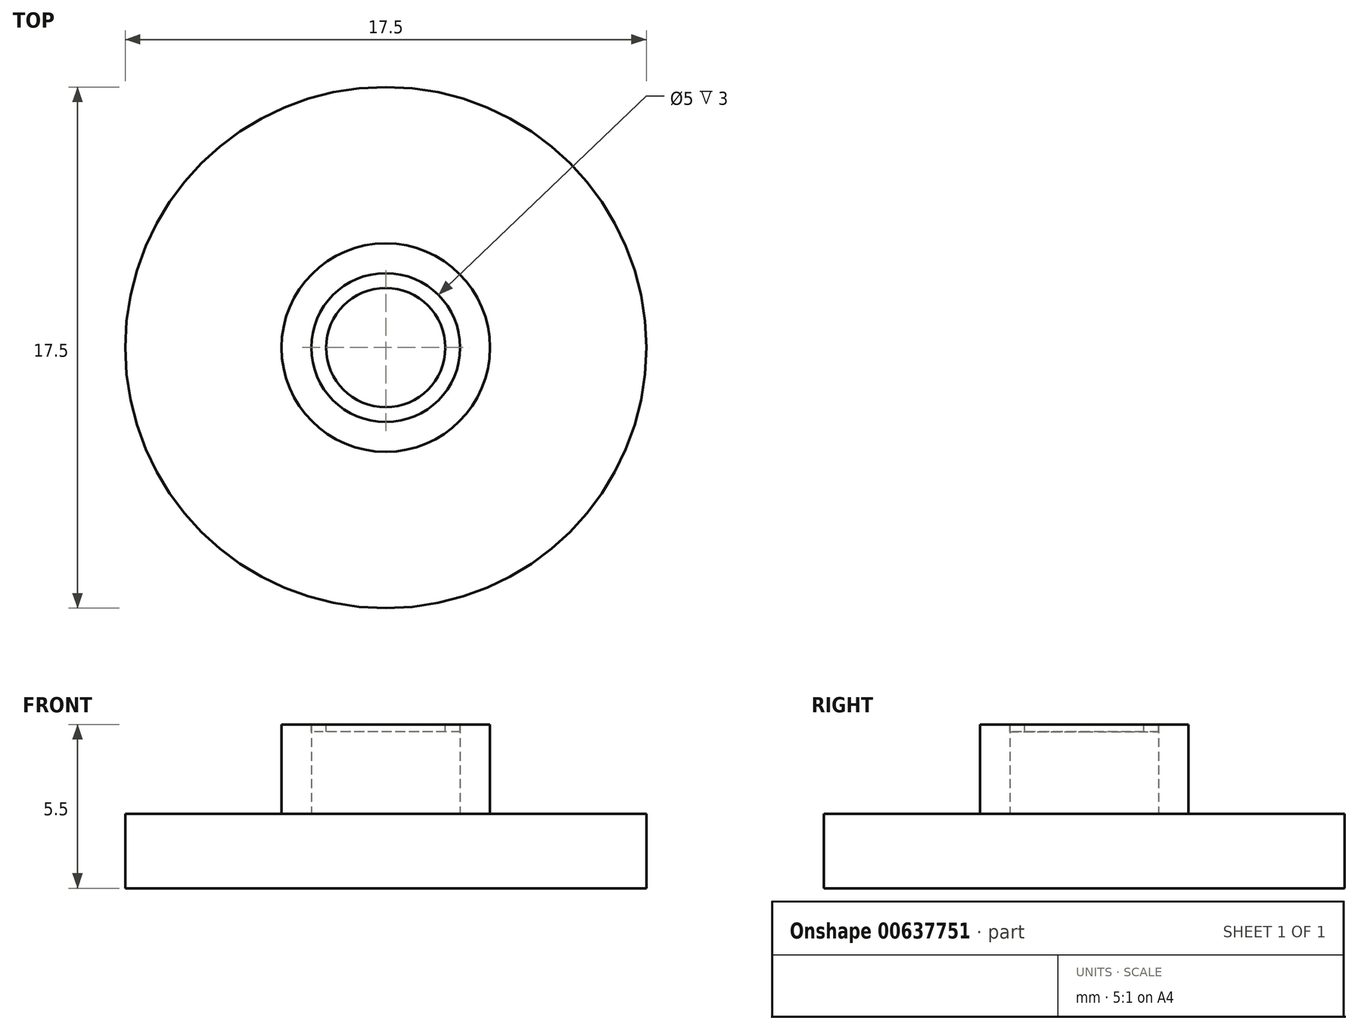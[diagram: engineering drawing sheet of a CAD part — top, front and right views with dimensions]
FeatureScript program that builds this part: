
annotation { "Feature Type Name" : "Feature", "Feature Type Description" : "" }
export const myFeature = defineFeature(function(context is Context, id is Id, definition is map)
    precondition{}
    {
        {
            var Q0;
            Q0=qCreatedBy(makeId("Top.planeOp"),FACE);
            var sketch = newSketch(context, id + "F0", { "sketchPlane" : qUnion([Q0])});
            skCircle(sketch, "E0", {"center": v(0, 0) * mm, "radius": 8.75 * mm});
            skSolve(sketch);
        }
        {
            var Q0;
            Q0=makeQuery(id+"F0.imprint","IMPRINT",FACE,{"disambiguationData":[TD([[makeQuery(id+"F0.imprint","IMPRINT",EDGE,{"derivedFrom":sQuery(id+"F0.wireOp",EDGE,"E0")}),1.0]])]});
            extrude(context, id + "F1", {"entities" : qUnion([Q0]), "depth" : 2.5 * mm, "offsetDistance" : 25.4 * mm});
        }
        {
            var Q0;
            Q0=makeQuery(id+"F1.opExtrude","CAP_FACE",FACE,{"disambiguationData":[OSD([sQuery(id+"F0.wireOp",EDGE,"E0")])],"isStart":false});
            var sketch = newSketch(context, id + "F2", { "sketchPlane" : qUnion([Q0])});
            skCircle(sketch, "E1", {"center": v(0, 0) * mm, "radius": 3.5 * mm});
            skCircle(sketch, "E2", {"center": v(0, 0) * mm, "radius": 2.5 * mm});
            skSolve(sketch);
        }
        {
            var Q0;
            Q0=makeQuery(id+"F2.imprint","IMPRINT",FACE,{"disambiguationData":[TD([[makeQuery(id+"F2.imprint","IMPRINT",EDGE,{"derivedFrom":sQuery(id+"F2.wireOp",EDGE,"E1")}),1.0]])]});
            extrude(context, id + "F3", {"entities" : qUnion([Q0]), "operationType" : NewBodyOperationType.ADD, "depth" : 3 * mm, "offsetDistance" : 25.4 * mm});
        }
        {
            var Q0;
            Q0=makeQuery(id+"F3.opExtrude","CAP_FACE",FACE,{"disambiguationData":[OSD([sQuery(id+"F2.wireOp",EDGE,"E1"),sQuery(id+"F2.wireOp",EDGE,"E2")])],"isStart":false});
            var sketch = newSketch(context, id + "F4", { "sketchPlane" : qUnion([Q0])});
            skCircle(sketch, "E3", {"center": v(0, 0) * mm, "radius": 50.8 * mm});
            skCircle(sketch, "E4", {"center": v(0, 0) * mm, "radius": 2 * mm});
            skCircle(sketch, "E5", {"center": v(0, 0) * mm, "radius": 2.5 * mm});
            skSolve(sketch);
        }
        {
            var Q0;
            Q0=makeQuery(id+"F4.imprint","IMPRINT",FACE,{"disambiguationData":[TD([[makeQuery(id+"F4.imprint","IMPRINT",EDGE,{"derivedFrom":sQuery(id+"F4.wireOp",EDGE,"E4")}),-1.0]])]});
            extrude(context, id + "F5", {"entities" : qUnion([Q0]), "oppositeDirection" : true, "depth" : .25 * mm, "offsetDistance" : 25.4 * mm});
        }
    });
